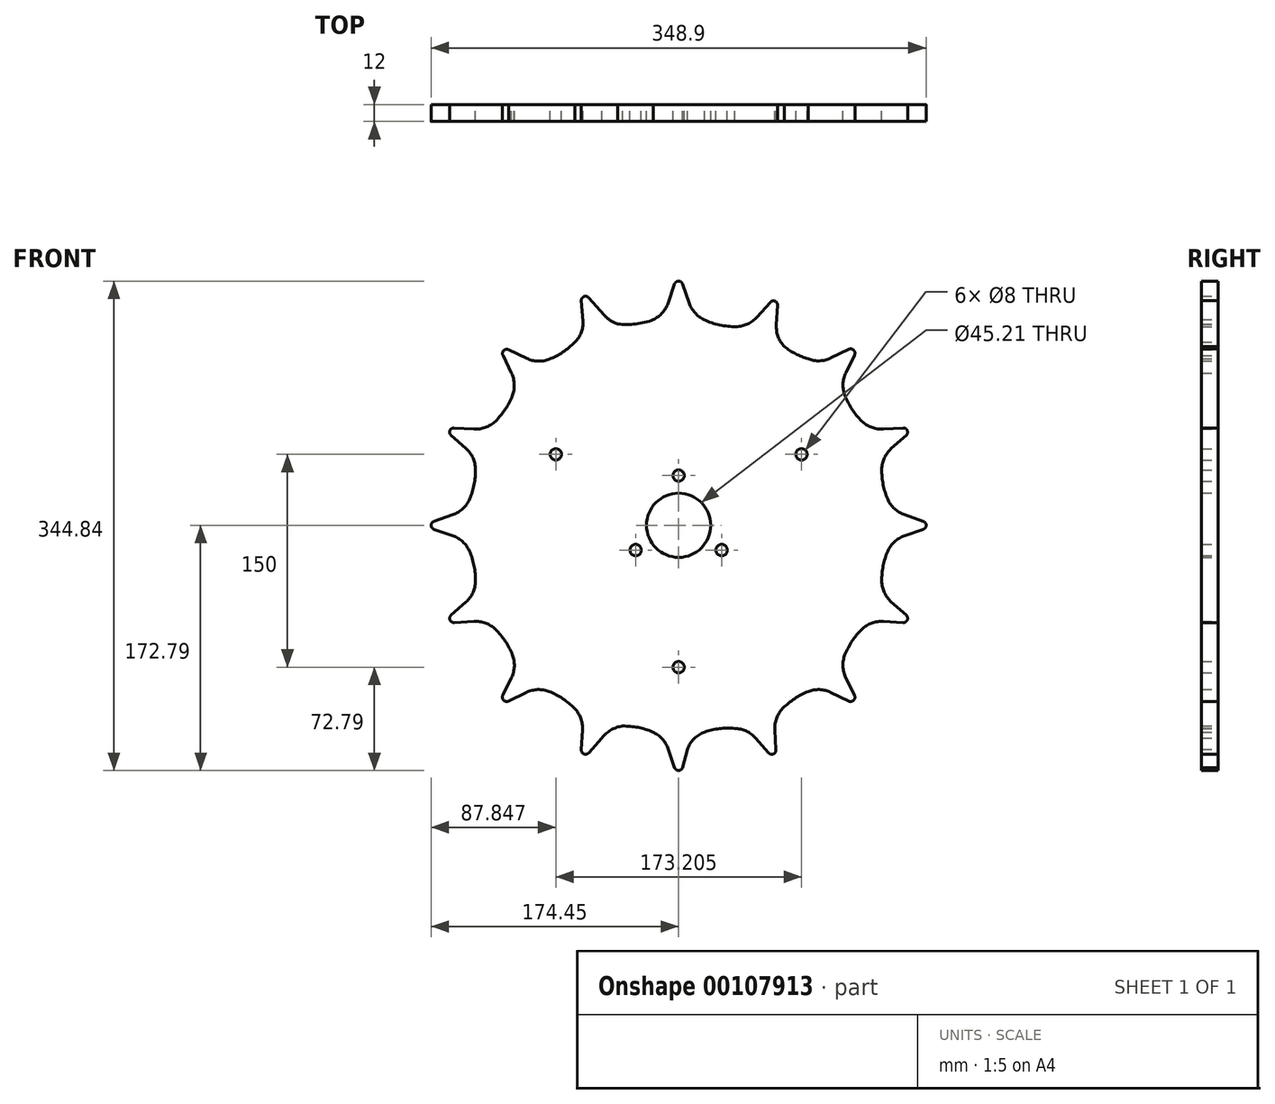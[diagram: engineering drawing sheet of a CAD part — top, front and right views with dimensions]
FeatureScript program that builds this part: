
annotation { "Feature Type Name" : "Feature", "Feature Type Description" : "" }
export const myFeature = defineFeature(function(context is Context, id is Id, definition is map)
    precondition{}
    {
        {
            var Q0;
            Q0=qCreatedBy(makeId("Front.planeOp"),FACE);
            var sketch = newSketch(context, id + "F0", { "sketchPlane" : qUnion([Q0])});
            skLineSegment(sketch, "E0", {"start": v(0, 0) * mm, "end": v(0, 169.05) * mm, "construction": true});
            skLineSegment(sketch, "E1", {"start": v(7.53, 156.46) * mm, "end": v(2.84, 170.03) * mm});
            skArc(sketch, "E2", {"start": v(17.8, 144.96) * mm, "mid": v(28.88, 141.16) * mm, "end": v(40.54, 140) * mm});
            skCircle(sketch, "E3", {"center": v(0, 0) * mm, "radius": 22.6 * mm});
            skCircle(sketch, "E4", {"center": v(0, 0) * mm, "radius": 150 * mm, "construction": true});
            skPoint(sketch, "E5", {"position": v(0, 150) * mm});
            skPoint(sketch, "E6.visualSharp", {"position": v(0, 169.05) * mm});
            skArc(sketch, "E6.filletArc", {"start": v(2.84, 170.03) * mm, "mid": v(0, 172.05) * mm, "end": v(-2.84, 170.03) * mm});
            skPoint(sketch, "E7.visualSharp", {"position": v(9.88, 149.67) * mm});
            skArc(sketch, "E7.filletArc", {"start": v(7.53, 156.46) * mm, "mid": v(11.51, 149.68) * mm, "end": v(17.8, 144.96) * mm});
            skLineSegment(sketch, "E8.MirrorCS", {"start": v(-7.53, 156.46) * mm, "end": v(-2.84, 170.03) * mm});
            skArc(sketch, "E9.MirrorCS", {"start": v(-7.53, 156.46) * mm, "mid": v(-11.51, 149.68) * mm, "end": v(-17.8, 144.96) * mm});
            skPoint(sketch, "E10.orphan", {"position": v(50.67, 141.18) * mm});
            skLineSegment(sketch, "E11", {"start": v(-26.43, 163) * mm, "end": v(26.43, 163) * mm, "construction": true});
            skPoint(sketch, "E12.orphan", {"position": v(-7.21, 149.83) * mm});
            skLineSegment(sketch, "E13", {"start": v(39.72, 190.79) * mm, "end": v(0, 0) * mm, "construction": true});
            skArc(sketch, "E14.1.1", {"start": v(-67.54, 143.68) * mm, "mid": v(-68.73, 135.7) * mm, "end": v(-73.24, 129.02) * mm});
            skLineSegment(sketch, "E14.1.2", {"start": v(-67.54, 143.68) * mm, "end": v(-68.6, 158.22) * mm});
            skLineSegment(sketch, "E14.1.3", {"start": v(-85.79, 142.34) * mm, "end": v(-35.88, 163) * mm, "construction": true});
            skArc(sketch, "E14.1.4", {"start": v(-63.37, 160.4) * mm, "mid": v(-66.76, 161.17) * mm, "end": v(-68.6, 158.22) * mm});
            skLineSegment(sketch, "E14.1.5", {"start": v(-52.56, 148.2) * mm, "end": v(-63.37, 160.4) * mm});
            skArc(sketch, "E14.1.6", {"start": v(-52.56, 148.2) * mm, "mid": v(-48.22, 144.44) * mm, "end": v(-43.07, 141.9) * mm});
            skLineSegment(sketch, "E14.1.7", {"start": v(-36.37, 192.53) * mm, "end": v(0, 0) * mm, "construction": true});
            skArc(sketch, "E14.1.8", {"start": v(-43.07, 141.9) * mm, "mid": v(-30.24, 141.83) * mm, "end": v(-17.8, 144.96) * mm});
            skPoint(sketch, "E14.1.9", {"position": v(-9.88, 152.08) * mm});
            skPoint(sketch, "E14.1.10", {"position": v(-49.07, 144.28) * mm});
            skPoint(sketch, "E14.1.11", {"position": v(-67.32, 136.72) * mm});
            skLineSegment(sketch, "E14.1.12", {"start": v(0, 0) * mm, "end": v(-65.61, 158.4) * mm, "construction": true});
            skArc(sketch, "E14.2.1", {"start": v(-117.84, 107.12) * mm, "mid": v(-115.86, 99.25) * mm, "end": v(-117.2, 91.25) * mm});
            skLineSegment(sketch, "E14.2.2", {"start": v(-117.84, 107.12) * mm, "end": v(-123.77, 119.64) * mm});
            skLineSegment(sketch, "E14.2.3", {"start": v(-135.69, 98.45) * mm, "end": v(-98.48, 135.66) * mm, "construction": true});
            skArc(sketch, "E14.2.4", {"start": v(-119.8, 123.8) * mm, "mid": v(-123.32, 123.18) * mm, "end": v(-123.77, 119.64) * mm});
            skLineSegment(sketch, "E14.2.5", {"start": v(-107.22, 117.67) * mm, "end": v(-119.8, 123.8) * mm});
            skArc(sketch, "E14.2.6", {"start": v(-107.22, 117.67) * mm, "mid": v(-99.24, 115.68) * mm, "end": v(-91.14, 117.05) * mm});
            skLineSegment(sketch, "E14.2.7", {"start": v(-109.77, 164.31) * mm, "end": v(0, 0) * mm, "construction": true});
            skArc(sketch, "E14.2.8", {"start": v(-91.14, 117.05) * mm, "mid": v(-81.55, 122.08) * mm, "end": v(-73.24, 129.02) * mm});
            skPoint(sketch, "E14.2.9", {"position": v(-67.32, 136.72) * mm});
            skPoint(sketch, "E14.2.10", {"position": v(-100.55, 114.52) * mm});
            skPoint(sketch, "E14.2.11", {"position": v(-114.52, 100.55) * mm});
            skLineSegment(sketch, "E14.2.12", {"start": v(0, 0) * mm, "end": v(-121.12, 121.1) * mm, "construction": true});
            skArc(sketch, "E15.1.3.0", {"start": v(-149.92, 54.08) * mm, "mid": v(-145.02, 47.47) * mm, "end": v(-143.2, 39.46) * mm});
            skLineSegment(sketch, "E15.5.3.0", {"start": v(-149.92, 54.08) * mm, "end": v(-160.4, 63.37) * mm});
            skLineSegment(sketch, "E15.8.3.0", {"start": v(-163.2, 39.12) * mm, "end": v(-143.05, 87.74) * mm, "construction": true});
            skArc(sketch, "E15.11.3.0", {"start": v(-158.22, 68.6) * mm, "mid": v(-161.17, 66.76) * mm, "end": v(-160.4, 63.37) * mm});
            skLineSegment(sketch, "E15.15.3.0", {"start": v(-144.25, 67.77) * mm, "end": v(-158.22, 68.6) * mm});
            skArc(sketch, "E15.18.3.0", {"start": v(-144.25, 67.77) * mm, "mid": v(-136.11, 68.98) * mm, "end": v(-129.16, 73.35) * mm});
            skLineSegment(sketch, "E15.22.3.0", {"start": v(-164.46, 109.89) * mm, "end": v(0, 0) * mm, "construction": true});
            skArc(sketch, "E15.25.3.0", {"start": v(-129.16, 73.35) * mm, "mid": v(-122.22, 81.66) * mm, "end": v(-117.2, 91.25) * mm});
            skPoint(sketch, "E15.30.3.0", {"position": v(-136.72, 67.32) * mm});
            skPoint(sketch, "E15.31.3.0", {"position": v(-144.28, 49.07) * mm});
            skLineSegment(sketch, "E15.32.3.0", {"start": v(0, 0) * mm, "end": v(-158.4, 65.61) * mm, "construction": true});
            skArc(sketch, "E15.1.4.0", {"start": v(-159.2, -7.41) * mm, "mid": v(-152.15, -11.64) * mm, "end": v(-147.4, -18.34) * mm});
            skLineSegment(sketch, "E15.5.4.0", {"start": v(-159.2, -7.41) * mm, "end": v(-172.43, -2.84) * mm});
            skLineSegment(sketch, "E15.8.4.0", {"start": v(-165.74, -26.31) * mm, "end": v(-165.74, 26.31) * mm, "construction": true});
            skArc(sketch, "E15.11.4.0", {"start": v(-172.43, 2.84) * mm, "mid": v(-174.45, 0) * mm, "end": v(-172.43, -2.84) * mm});
            skLineSegment(sketch, "E15.15.4.0", {"start": v(-159.2, 7.41) * mm, "end": v(-172.43, 2.84) * mm});
            skArc(sketch, "E15.18.4.0", {"start": v(-159.2, 7.41) * mm, "mid": v(-152.15, 11.64) * mm, "end": v(-147.4, 18.34) * mm});
            skLineSegment(sketch, "E15.22.4.0", {"start": v(-193.99, 38.59) * mm, "end": v(0, 0) * mm, "construction": true});
            skArc(sketch, "E15.25.4.0", {"start": v(-147.4, 18.34) * mm, "mid": v(-144.16, 28.68) * mm, "end": v(-143.2, 39.46) * mm});
            skPoint(sketch, "E15.29.4.0", {"position": v(-144.28, 49.07) * mm});
            skPoint(sketch, "E15.30.4.0", {"position": v(-152.08, 9.88) * mm});
            skPoint(sketch, "E15.31.4.0", {"position": v(-152.08, -9.88) * mm});
            skLineSegment(sketch, "E15.32.4.0", {"start": v(0, 0) * mm, "end": v(-171.45, 0) * mm, "construction": true});
            skArc(sketch, "E15.1.5.0", {"start": v(-144.25, -67.77) * mm, "mid": v(-136.11, -68.98) * mm, "end": v(-129.16, -73.35) * mm});
            skLineSegment(sketch, "E15.5.5.0", {"start": v(-144.25, -67.77) * mm, "end": v(-158.22, -68.6) * mm});
            skLineSegment(sketch, "E15.8.5.0", {"start": v(-143.05, -87.74) * mm, "end": v(-163.2, -39.12) * mm, "construction": true});
            skArc(sketch, "E15.11.5.0", {"start": v(-160.4, -63.37) * mm, "mid": v(-161.17, -66.76) * mm, "end": v(-158.22, -68.6) * mm});
            skLineSegment(sketch, "E15.15.5.0", {"start": v(-149.92, -54.08) * mm, "end": v(-160.4, -63.37) * mm});
            skArc(sketch, "E15.18.5.0", {"start": v(-149.92, -54.08) * mm, "mid": v(-145.02, -47.47) * mm, "end": v(-143.2, -39.46) * mm});
            skLineSegment(sketch, "E15.22.5.0", {"start": v(-193.99, -38.59) * mm, "end": v(0, 0) * mm, "construction": true});
            skArc(sketch, "E15.25.5.0", {"start": v(-143.2, -39.46) * mm, "mid": v(-144.16, -28.68) * mm, "end": v(-147.4, -18.34) * mm});
            skPoint(sketch, "E15.29.5.0", {"position": v(-152.08, -9.88) * mm});
            skPoint(sketch, "E15.30.5.0", {"position": v(-144.28, -49.07) * mm});
            skPoint(sketch, "E15.31.5.0", {"position": v(-136.72, -67.32) * mm});
            skLineSegment(sketch, "E15.32.5.0", {"start": v(0, 0) * mm, "end": v(-158.4, -65.61) * mm, "construction": true});
            skArc(sketch, "E15.1.6.0", {"start": v(-107.33, -117.81) * mm, "mid": v(-99.36, -115.82) * mm, "end": v(-91.25, -117.2) * mm});
            skLineSegment(sketch, "E15.5.6.0", {"start": v(-107.33, -117.81) * mm, "end": v(-119.92, -123.93) * mm});
            skLineSegment(sketch, "E15.8.6.0", {"start": v(-98.59, -135.8) * mm, "end": v(-135.8, -98.59) * mm, "construction": true});
            skArc(sketch, "E15.11.6.0", {"start": v(-123.93, -119.92) * mm, "mid": v(-123.35, -123.35) * mm, "end": v(-119.92, -123.93) * mm});
            skLineSegment(sketch, "E15.15.6.0", {"start": v(-117.81, -107.33) * mm, "end": v(-123.93, -119.92) * mm});
            skArc(sketch, "E15.18.6.0", {"start": v(-117.81, -107.33) * mm, "mid": v(-115.82, -99.36) * mm, "end": v(-117.2, -91.25) * mm});
            skLineSegment(sketch, "E15.22.6.0", {"start": v(-164.46, -109.89) * mm, "end": v(0, 0) * mm, "construction": true});
            skArc(sketch, "E15.25.6.0", {"start": v(-117.2, -91.25) * mm, "mid": v(-122.22, -81.66) * mm, "end": v(-129.16, -73.35) * mm});
            skPoint(sketch, "E15.29.6.0", {"position": v(-136.72, -67.32) * mm});
            skPoint(sketch, "E15.30.6.0", {"position": v(-114.52, -100.55) * mm});
            skPoint(sketch, "E15.31.6.0", {"position": v(-100.55, -114.52) * mm});
            skLineSegment(sketch, "E15.32.6.0", {"start": v(0, 0) * mm, "end": v(-121.23, -121.23) * mm, "construction": true});
            skArc(sketch, "E15.1.7.0", {"start": v(-54.08, -149.92) * mm, "mid": v(-47.62, -144.25) * mm, "end": v(-39.46, -141.54) * mm});
            skLineSegment(sketch, "E15.5.7.0", {"start": v(-54.08, -149.92) * mm, "end": v(-63.37, -160.4) * mm});
            skLineSegment(sketch, "E15.8.7.0", {"start": v(-36.84, -163.04) * mm, "end": v(-87.74, -143.05) * mm, "construction": true});
            skArc(sketch, "E15.11.7.0", {"start": v(-68.6, -158.22) * mm, "mid": v(-66.76, -161.17) * mm, "end": v(-63.37, -160.4) * mm});
            skLineSegment(sketch, "E15.15.7.0", {"start": v(-67.77, -144.25) * mm, "end": v(-68.6, -158.22) * mm});
            skArc(sketch, "E15.18.7.0", {"start": v(-67.77, -144.25) * mm, "mid": v(-68.98, -136.11) * mm, "end": v(-73.35, -129.16) * mm});
            skLineSegment(sketch, "E15.22.7.0", {"start": v(-109.89, -164.46) * mm, "end": v(0, 0) * mm, "construction": true});
            skArc(sketch, "E15.25.7.0", {"start": v(-73.35, -129.16) * mm, "mid": v(-81.66, -122.22) * mm, "end": v(-91.25, -117.2) * mm});
            skPoint(sketch, "E15.29.7.0", {"position": v(-100.55, -114.52) * mm});
            skPoint(sketch, "E15.30.7.0", {"position": v(-67.32, -136.72) * mm});
            skPoint(sketch, "E15.31.7.0", {"position": v(-49.07, -144.28) * mm});
            skLineSegment(sketch, "E15.32.7.0", {"start": v(0, 0) * mm, "end": v(-65.61, -158.4) * mm, "construction": true});
            skArc(sketch, "E15.1.8.0", {"start": v(6.23, -157.86) * mm, "mid": v(10.92, -150.44) * mm, "end": v(18.34, -145.74) * mm});
            skLineSegment(sketch, "E15.5.8.0", {"start": v(6.23, -157.86) * mm, "end": v(2.84, -170.77) * mm});
            skLineSegment(sketch, "E15.8.8.0", {"start": v(25.07, -164.57) * mm, "end": v(-26.31, -164.08) * mm, "construction": true});
            skArc(sketch, "E15.11.8.0", {"start": v(-2.84, -170.77) * mm, "mid": v(0, -172.8) * mm, "end": v(2.84, -170.77) * mm});
            skLineSegment(sketch, "E15.15.8.0", {"start": v(-7.41, -157.54) * mm, "end": v(-2.84, -170.77) * mm});
            skArc(sketch, "E15.18.8.0", {"start": v(-7.41, -157.54) * mm, "mid": v(-11.64, -150.5) * mm, "end": v(-18.34, -145.74) * mm});
            skLineSegment(sketch, "E15.22.8.0", {"start": v(-38.59, -192.33) * mm, "end": v(0, 0) * mm, "construction": true});
            skArc(sketch, "E15.25.8.0", {"start": v(-18.34, -145.74) * mm, "mid": v(-28.68, -142.5) * mm, "end": v(-39.46, -141.54) * mm});
            skPoint(sketch, "E15.29.8.0", {"position": v(-49.07, -144.28) * mm});
            skPoint(sketch, "E15.30.8.0", {"position": v(-9.88, -152.08) * mm});
            skPoint(sketch, "E15.31.8.0", {"position": v(9.88, -152.08) * mm});
            skLineSegment(sketch, "E15.32.8.0", {"start": v(0, 0) * mm, "end": v(0, -169.8) * mm, "construction": true});
            skArc(sketch, "E15.1.9.0", {"start": v(67.77, -144.25) * mm, "mid": v(68.98, -136.11) * mm, "end": v(73.35, -129.16) * mm});
            skLineSegment(sketch, "E15.5.9.0", {"start": v(67.77, -144.25) * mm, "end": v(68.6, -158.22) * mm});
            skLineSegment(sketch, "E15.8.9.0", {"start": v(87.74, -143.05) * mm, "end": v(39.12, -163.2) * mm, "construction": true});
            skArc(sketch, "E15.11.9.0", {"start": v(63.37, -160.4) * mm, "mid": v(66.76, -161.17) * mm, "end": v(68.6, -158.22) * mm});
            skLineSegment(sketch, "E15.15.9.0", {"start": v(54.08, -149.92) * mm, "end": v(63.37, -160.4) * mm});
            skArc(sketch, "E15.18.9.0", {"start": v(54.08, -149.92) * mm, "mid": v(47.47, -145.02) * mm, "end": v(39.46, -143.2) * mm});
            skLineSegment(sketch, "E15.22.9.0", {"start": v(34.84, -193.79) * mm, "end": v(0, 0) * mm, "construction": true});
            skArc(sketch, "E15.25.9.0", {"start": v(39.46, -143.2) * mm, "mid": v(28.77, -143.35) * mm, "end": v(18.34, -145.74) * mm});
            skPoint(sketch, "E15.29.9.0", {"position": v(9.88, -152.08) * mm});
            skPoint(sketch, "E15.30.9.0", {"position": v(49.07, -144.28) * mm});
            skPoint(sketch, "E15.31.9.0", {"position": v(67.32, -136.72) * mm});
            skLineSegment(sketch, "E15.32.9.0", {"start": v(0, 0) * mm, "end": v(65.61, -158.4) * mm, "construction": true});
            skArc(sketch, "E15.1.10.0", {"start": v(117.81, -107.33) * mm, "mid": v(115.82, -99.36) * mm, "end": v(117.2, -91.25) * mm});
            skLineSegment(sketch, "E15.5.10.0", {"start": v(117.81, -107.33) * mm, "end": v(123.93, -119.92) * mm});
            skLineSegment(sketch, "E15.8.10.0", {"start": v(135.8, -98.59) * mm, "end": v(98.59, -135.8) * mm, "construction": true});
            skArc(sketch, "E15.11.10.0", {"start": v(119.92, -123.93) * mm, "mid": v(123.35, -123.35) * mm, "end": v(123.93, -119.92) * mm});
            skLineSegment(sketch, "E15.15.10.0", {"start": v(107.33, -117.81) * mm, "end": v(119.92, -123.93) * mm});
            skArc(sketch, "E15.18.10.0", {"start": v(107.33, -117.81) * mm, "mid": v(99.36, -115.82) * mm, "end": v(91.25, -117.2) * mm});
            skLineSegment(sketch, "E15.22.10.0", {"start": v(109.89, -164.46) * mm, "end": v(0, 0) * mm, "construction": true});
            skArc(sketch, "E15.25.10.0", {"start": v(91.25, -117.2) * mm, "mid": v(81.66, -122.22) * mm, "end": v(73.35, -129.16) * mm});
            skPoint(sketch, "E15.29.10.0", {"position": v(67.32, -136.72) * mm});
            skPoint(sketch, "E15.30.10.0", {"position": v(100.55, -114.52) * mm});
            skPoint(sketch, "E15.31.10.0", {"position": v(114.52, -100.55) * mm});
            skLineSegment(sketch, "E15.32.10.0", {"start": v(0, 0) * mm, "end": v(121.23, -121.23) * mm, "construction": true});
            skArc(sketch, "E15.1.11.0", {"start": v(149.92, -54.08) * mm, "mid": v(145.02, -47.47) * mm, "end": v(143.2, -39.46) * mm});
            skLineSegment(sketch, "E15.5.11.0", {"start": v(149.92, -54.08) * mm, "end": v(160.4, -63.37) * mm});
            skLineSegment(sketch, "E15.8.11.0", {"start": v(163.2, -39.12) * mm, "end": v(143.05, -87.74) * mm, "construction": true});
            skArc(sketch, "E15.11.11.0", {"start": v(158.22, -68.6) * mm, "mid": v(161.17, -66.76) * mm, "end": v(160.4, -63.37) * mm});
            skLineSegment(sketch, "E15.15.11.0", {"start": v(144.25, -67.77) * mm, "end": v(158.22, -68.6) * mm});
            skArc(sketch, "E15.18.11.0", {"start": v(144.25, -67.77) * mm, "mid": v(136.11, -68.98) * mm, "end": v(129.16, -73.35) * mm});
            skLineSegment(sketch, "E15.22.11.0", {"start": v(164.46, -109.89) * mm, "end": v(0, 0) * mm, "construction": true});
            skArc(sketch, "E15.25.11.0", {"start": v(129.16, -73.35) * mm, "mid": v(122.22, -81.66) * mm, "end": v(117.2, -91.25) * mm});
            skPoint(sketch, "E15.29.11.0", {"position": v(114.52, -100.55) * mm});
            skPoint(sketch, "E15.30.11.0", {"position": v(136.72, -67.32) * mm});
            skPoint(sketch, "E15.31.11.0", {"position": v(144.28, -49.07) * mm});
            skLineSegment(sketch, "E15.32.11.0", {"start": v(0, 0) * mm, "end": v(158.4, -65.61) * mm, "construction": true});
            skArc(sketch, "E15.1.12.0", {"start": v(159.2, 7.41) * mm, "mid": v(152.15, 11.64) * mm, "end": v(147.4, 18.34) * mm});
            skLineSegment(sketch, "E15.5.12.0", {"start": v(159.2, 7.41) * mm, "end": v(172.43, 2.84) * mm});
            skLineSegment(sketch, "E15.8.12.0", {"start": v(165.74, 26.31) * mm, "end": v(165.74, -26.31) * mm, "construction": true});
            skArc(sketch, "E15.11.12.0", {"start": v(172.43, -2.84) * mm, "mid": v(174.45, 0) * mm, "end": v(172.43, 2.84) * mm});
            skLineSegment(sketch, "E15.15.12.0", {"start": v(159.2, -7.41) * mm, "end": v(172.43, -2.84) * mm});
            skArc(sketch, "E15.18.12.0", {"start": v(159.2, -7.41) * mm, "mid": v(152.15, -11.64) * mm, "end": v(147.4, -18.34) * mm});
            skLineSegment(sketch, "E15.22.12.0", {"start": v(193.99, -38.59) * mm, "end": v(0, 0) * mm, "construction": true});
            skArc(sketch, "E15.25.12.0", {"start": v(147.4, -18.34) * mm, "mid": v(144.16, -28.68) * mm, "end": v(143.2, -39.46) * mm});
            skPoint(sketch, "E15.29.12.0", {"position": v(144.28, -49.07) * mm});
            skPoint(sketch, "E15.30.12.0", {"position": v(152.08, -9.88) * mm});
            skPoint(sketch, "E15.31.12.0", {"position": v(152.08, 9.88) * mm});
            skLineSegment(sketch, "E15.32.12.0", {"start": v(0, 0) * mm, "end": v(171.45, 0) * mm, "construction": true});
            skArc(sketch, "E15.1.13.0", {"start": v(144.25, 67.77) * mm, "mid": v(136.11, 68.98) * mm, "end": v(129.16, 73.35) * mm});
            skLineSegment(sketch, "E15.5.13.0", {"start": v(144.25, 67.77) * mm, "end": v(158.22, 68.6) * mm});
            skLineSegment(sketch, "E15.8.13.0", {"start": v(143.05, 87.74) * mm, "end": v(163.2, 39.12) * mm, "construction": true});
            skArc(sketch, "E15.11.13.0", {"start": v(160.4, 63.37) * mm, "mid": v(161.17, 66.76) * mm, "end": v(158.22, 68.6) * mm});
            skLineSegment(sketch, "E15.15.13.0", {"start": v(149.92, 54.08) * mm, "end": v(160.4, 63.37) * mm});
            skArc(sketch, "E15.18.13.0", {"start": v(149.92, 54.08) * mm, "mid": v(145.02, 47.47) * mm, "end": v(143.2, 39.46) * mm});
            skLineSegment(sketch, "E15.22.13.0", {"start": v(193.99, 38.59) * mm, "end": v(0, 0) * mm, "construction": true});
            skArc(sketch, "E15.25.13.0", {"start": v(143.2, 39.46) * mm, "mid": v(144.16, 28.68) * mm, "end": v(147.4, 18.34) * mm});
            skPoint(sketch, "E15.29.13.0", {"position": v(152.08, 9.88) * mm});
            skPoint(sketch, "E15.30.13.0", {"position": v(144.28, 49.07) * mm});
            skPoint(sketch, "E15.31.13.0", {"position": v(136.72, 67.32) * mm});
            skLineSegment(sketch, "E15.32.13.0", {"start": v(0, 0) * mm, "end": v(158.4, 65.61) * mm, "construction": true});
            skArc(sketch, "E15.1.14.0", {"start": v(107.36, 117.9) * mm, "mid": v(99.38, 115.9) * mm, "end": v(91.28, 117.28) * mm});
            skLineSegment(sketch, "E15.5.14.0", {"start": v(107.36, 117.9) * mm, "end": v(119.95, 124.02) * mm});
            skLineSegment(sketch, "E15.8.14.0", {"start": v(98.61, 135.89) * mm, "end": v(135.83, 98.68) * mm, "construction": true});
            skArc(sketch, "E15.11.14.0", {"start": v(123.96, 120) * mm, "mid": v(123.38, 123.44) * mm, "end": v(119.95, 124.02) * mm});
            skLineSegment(sketch, "E15.15.14.0", {"start": v(117.84, 107.42) * mm, "end": v(123.96, 120) * mm});
            skArc(sketch, "E15.18.14.0", {"start": v(117.84, 107.42) * mm, "mid": v(115.84, 99.44) * mm, "end": v(117.22, 91.34) * mm});
            skLineSegment(sketch, "E15.22.14.0", {"start": v(164.55, 109.8) * mm, "end": v(0, 0) * mm, "construction": true});
            skArc(sketch, "E15.25.14.0", {"start": v(117.22, 91.34) * mm, "mid": v(122.22, 81.7) * mm, "end": v(129.16, 73.35) * mm});
            skPoint(sketch, "E15.29.14.0", {"position": v(136.72, 67.32) * mm});
            skPoint(sketch, "E15.30.14.0", {"position": v(114.52, 100.55) * mm});
            skPoint(sketch, "E15.31.14.0", {"position": v(100.55, 114.52) * mm});
            skLineSegment(sketch, "E15.32.14.0", {"start": v(0, 0) * mm, "end": v(121.26, 121.32) * mm, "construction": true});
            skArc(sketch, "E15.1.15.0", {"start": v(55.2, 146.72) * mm, "mid": v(48.58, 141.81) * mm, "end": v(40.54, 140) * mm});
            skLineSegment(sketch, "E15.5.15.0", {"start": v(55.2, 146.72) * mm, "end": v(64.5, 157.19) * mm});
            skLineSegment(sketch, "E15.8.15.0", {"start": v(40.25, 160) * mm, "end": v(88.87, 139.85) * mm, "construction": true});
            skArc(sketch, "E15.11.15.0", {"start": v(69.74, 155.02) * mm, "mid": v(67.9, 157.97) * mm, "end": v(64.5, 157.19) * mm});
            skLineSegment(sketch, "E15.15.15.0", {"start": v(68.9, 141.04) * mm, "end": v(69.74, 155.02) * mm});
            skArc(sketch, "E15.18.15.0", {"start": v(68.9, 141.04) * mm, "mid": v(70.1, 132.91) * mm, "end": v(74.48, 125.95) * mm});
            skLineSegment(sketch, "E15.22.15.0", {"start": v(105.74, 165.89) * mm, "end": v(0, 0) * mm, "construction": true});
            skArc(sketch, "E15.25.15.0", {"start": v(74.48, 125.95) * mm, "mid": v(82.47, 120.83) * mm, "end": v(91.28, 117.28) * mm});
            skPoint(sketch, "E15.29.15.0", {"position": v(100.55, 114.52) * mm});
            skPoint(sketch, "E15.30.15.0", {"position": v(67.32, 136.72) * mm});
            skPoint(sketch, "E15.31.15.0", {"position": v(49.07, 144.28) * mm});
            skLineSegment(sketch, "E15.32.15.0", {"start": v(0, 0) * mm, "end": v(66.74, 155.2) * mm, "construction": true});
            skCircle(sketch, "E16", {"center": v(0, 35) * mm, "radius": 4 * mm});
            skCircle(sketch, "E17", {"center": v(0, -100) * mm, "radius": 4 * mm});
            skCircle(sketch, "E18.1.0", {"center": v(-30.31, -17.5) * mm, "radius": 4 * mm});
            skCircle(sketch, "E18.2.0", {"center": v(30.31, -17.5) * mm, "radius": 4 * mm});
            skCircle(sketch, "E19.1.0", {"center": v(86.6, 50) * mm, "radius": 4 * mm});
            skCircle(sketch, "E19.2.0", {"center": v(-86.6, 50) * mm, "radius": 4 * mm});
            skSolve(sketch);
        }
        {
            var Q0;
            Q0 = qSketchRegion(id + "F0", true);
            extrude(context, id + "F1", {"entities" : qUnion([Q0]), "depth" : 12 * mm, "offsetDistance" : 25 * mm});
        }
    });
